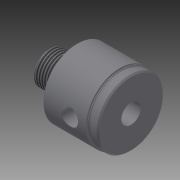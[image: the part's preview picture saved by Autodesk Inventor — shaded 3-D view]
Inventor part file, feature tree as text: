
AUTODESK INVENTOR PART (.ipt)
format: ipt  version: 2014 (Build 180170000, 170)  size: 252,416 bytes
history: native  units: in
note: dims shown in document units (in); Inventor stores cm internally (conversion verified against a paired STEP export)
features: other x112, sketch x5, revolve x4, thread x1, hole x1
ambient origin geometry x8: Origin, YZ Plane, XZ Plane, XY Plane, X Axis, Y Axis, Z Axis, Center Point
bodies: Solid1 (feature_tree)
feature tree (123):
  revolve  "Revolution1"  [1 undecoded]
  thread  "Thread1"  [1 undecoded]
  revolve  "Revolution2"  Angle=360.0deg
  hole  "Hole1"  [1 undecoded]
  revolve  "Revolution3"  [1 undecoded]
  revolve  "Revolution4"  [1 undecoded]
  other  "dp1_XY"
  other  "dp1_YZ"
  other  "dp1_ZX"
  other  "dp1_X"
  other  "dp1_Y"
  other  "dp1_Z"
  other  "dp1_Center"
  other  "dp2_XY"
  other  "dp2_YZ"
  other  "dp2_ZX"
  other  "dp2_X"
  other  "dp2_Y"
  other  "dp2_Z"
  other  "dp2_Center"
  other  "port_XY"
  other  "port_YZ"
  other  "port_ZX"
  other  "port_X"
  other  "port_Y"
  other  "port_Z"
  other  "port_Center"
  other  "rod_guide_XY"
  other  "rod_guide_YZ"
  other  "rod_guide_ZX"
  other  "rod_guide_X"
  other  "rod_guide_Y"
  other  "rod_guide_Z"
  other  "rod_guide_Center"
  other  "s1_XY"
  other  "s1_YZ"
  other  "s1_ZX"
  other  "s1_X"
  other  "s1_Y"
  other  "s1_Z"
  other  "s1_Center"
  other  "s2_XY"
  other  "s2_YZ"
  other  "s2_ZX"
  other  "s2_X"
  other  "s2_Y"
  other  "s2_Z"
  other  "s2_Center"
  other  "t1_XY"
  other  "t1_YZ"
  other  "t1_ZX"
  other  "t1_X"
  other  "t1_Y"
  other  "t1_Z"
  other  "t1_Center"
  other  "t111_XY"
  other  "t111_YZ"
  other  "t111_ZX"
  other  "t111_X"
  other  "t111_Y"
  other  "t111_Z"
  other  "t111_Center"
  other  "to_foot_bracket_XY"
  other  "to_foot_bracket_YZ"
  other  "to_foot_bracket_ZX"
  other  "to_foot_bracket_X"
  other  "to_foot_bracket_Y"
  other  "to_foot_bracket_Z"
  other  "to_foot_bracket_Center"
  other  "to_nut_XY"
  other  "to_nut_YZ"
  other  "to_nut_ZX"
  other  "to_nut_X"
  other  "to_nut_Y"
  other  "to_nut_Z"
  other  "to_nut_Center"
  other  "to_rod_XY"
  other  "to_rod_YZ"
  other  "to_rod_ZX"
  other  "to_rod_X"
  other  "to_rod_Y"
  other  "to_rod_Z"
  other  "to_rod_Center"
  other  "to_screw_XY"
  other  "to_screw_YZ"
  other  "to_screw_ZX"
  other  "to_screw_X"
  other  "to_screw_Y"
  other  "to_screw_Z"
  other  "to_screw_Center"
  other  "to_trunnion_brackets_XY"
  other  "to_trunnion_brackets_YZ"
  other  "to_trunnion_brackets_ZX"
  other  "to_trunnion_brackets_X"
  other  "to_trunnion_brackets_Y"
  other  "to_trunnion_brackets_Z"
  other  "to_trunnion_brackets_Center"
  other  "to_trunnion_brackets1_XY"
  other  "to_trunnion_brackets1_YZ"
  other  "to_trunnion_brackets1_ZX"
  other  "to_trunnion_brackets1_X"
  other  "to_trunnion_brackets1_Y"
  other  "to_trunnion_brackets1_Z"
  other  "to_trunnion_brackets1_Center"
  other  "to_trunnion_brackets2_XY"
  other  "to_trunnion_brackets2_YZ"
  other  "to_trunnion_brackets2_ZX"
  other  "to_trunnion_brackets2_X"
  other  "to_trunnion_brackets2_Y"
  other  "to_trunnion_brackets2_Z"
  other  "to_trunnion_brackets2_Center"
  other  "to_tube_XY"
  other  "to_tube_YZ"
  other  "to_tube_ZX"
  other  "to_tube_X"
  other  "to_tube_Y"
  other  "to_tube_Z"
  other  "to_tube_Center"
  sketch  "Sketch_2"  dims[d0=360.0deg d1=0.3297in d2=0.0in d3=360.0deg]
  sketch  "Sketch_3"  dims[d4=0.442in d5=0.75in d6=0.502in d7=0.25in d8=90.0deg d9=1.875in d10=0.0in d11=360.0deg]
  sketch  "Sketch3"  dims[d12=360.0deg]
  sketch  "Sketch_40"
  sketch  "Sketch_47"
note: 5 required parameter values undecoded (feature->parameter linkage not recoverable at this tier; creation-order binding heuristic only, values carry confidence <= 0.55)